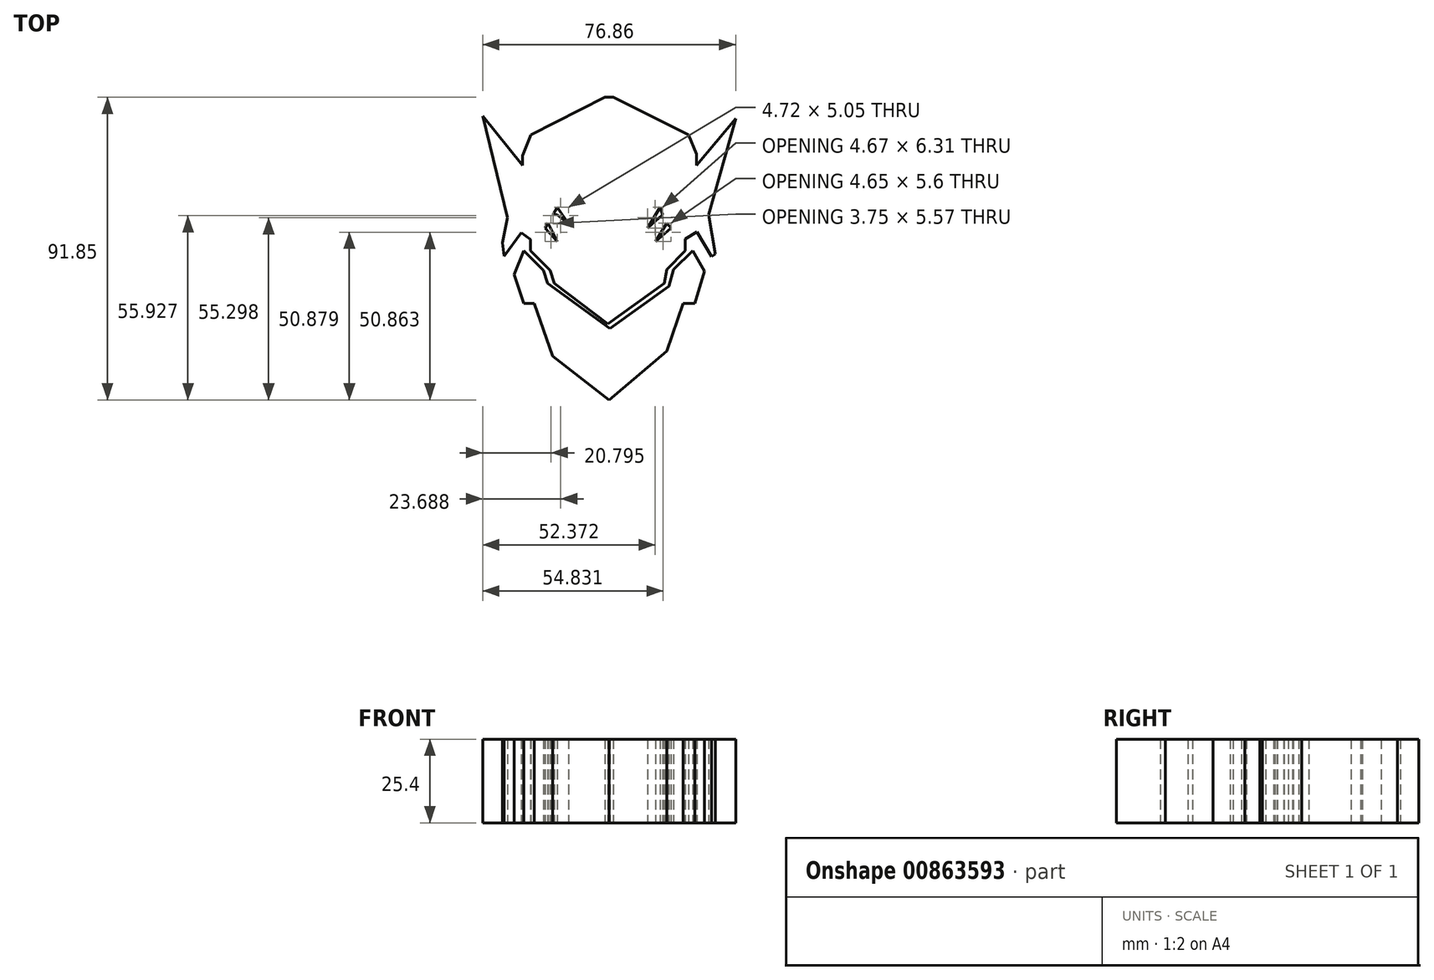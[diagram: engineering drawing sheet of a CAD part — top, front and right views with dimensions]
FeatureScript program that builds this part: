
annotation { "Feature Type Name" : "Feature", "Feature Type Description" : "" }
export const myFeature = defineFeature(function(context is Context, id is Id, definition is map)
    precondition{}
    {
        {
            var Q0;
            Q0=qCreatedBy(makeId("Top.planeOp"),FACE);
            var sketch = newSketch(context, id + "F0", { "sketchPlane" : qUnion([Q0])});
            skLineSegment(sketch, "E0", {"start": v(-37.07, 44.48) * mm, "end": v(-29.57, 13.63) * mm});
            skLineSegment(sketch, "E1", {"start": v(-29.57, 13.63) * mm, "end": v(-31.1, 5.96) * mm});
            skLineSegment(sketch, "E2", {"start": v(-31.1, 5.96) * mm, "end": v(-30.59, 1.87) * mm});
            skLineSegment(sketch, "E3", {"start": v(-30.59, 1.87) * mm, "end": v(-25.3, 9.03) * mm});
            skLineSegment(sketch, "E4", {"start": v(-25.3, 9.03) * mm, "end": v(-22.54, 6.99) * mm});
            skLineSegment(sketch, "E5", {"start": v(-22.54, 6.99) * mm, "end": v(-22.54, 3.58) * mm});
            skLineSegment(sketch, "E6", {"start": v(-22.54, 3.58) * mm, "end": v(-16.62, -2.39) * mm});
            skLineSegment(sketch, "E7", {"start": v(-16.62, -2.39) * mm, "end": v(-15.25, -6.3) * mm});
            skLineSegment(sketch, "E8", {"start": v(-15.25, -6.3) * mm, "end": v(0.9, -18.64) * mm});
            skLineSegment(sketch, "E9", {"start": v(0.9, -18.64) * mm, "end": v(18.07, -6.3) * mm});
            skLineSegment(sketch, "E10", {"start": v(18.07, -6.3) * mm, "end": v(18.83, -2.22) * mm});
            skLineSegment(sketch, "E11", {"start": v(18.83, -2.22) * mm, "end": v(24.45, 3.58) * mm});
            skLineSegment(sketch, "E12", {"start": v(24.45, 3.58) * mm, "end": v(24.45, 7.12) * mm});
            skLineSegment(sketch, "E13", {"start": v(24.45, 7.12) * mm, "end": v(27.95, 9.22) * mm});
            skLineSegment(sketch, "E14", {"start": v(27.95, 9.22) * mm, "end": v(32.39, 1.83) * mm});
            skLineSegment(sketch, "E15", {"start": v(32.39, 1.83) * mm, "end": v(33.6, 2.55) * mm});
            skLineSegment(sketch, "E16", {"start": v(33.6, 2.55) * mm, "end": v(31.61, 14.49) * mm});
            skLineSegment(sketch, "E17", {"start": v(31.61, 14.49) * mm, "end": v(39.8, 43.63) * mm});
            skLineSegment(sketch, "E18", {"start": v(39.8, 43.63) * mm, "end": v(27.86, 29.48) * mm});
            skLineSegment(sketch, "E19", {"start": v(27.86, 29.48) * mm, "end": v(27.86, 32.9) * mm});
            skLineSegment(sketch, "E20", {"start": v(27.86, 32.9) * mm, "end": v(25.48, 38.68) * mm});
            skLineSegment(sketch, "E21", {"start": v(25.48, 38.68) * mm, "end": v(2.64, 50.1) * mm});
            skLineSegment(sketch, "E22", {"start": v(2.64, 50.1) * mm, "end": v(0, 50.1) * mm});
            skLineSegment(sketch, "E23", {"start": v(0, 50.1) * mm, "end": v(-22.4, 38.68) * mm});
            skLineSegment(sketch, "E24", {"start": v(-22.4, 38.68) * mm, "end": v(-24.97, 32.38) * mm});
            skLineSegment(sketch, "E25", {"start": v(-24.97, 32.38) * mm, "end": v(-24.97, 29.48) * mm});
            skLineSegment(sketch, "E26", {"start": v(-24.97, 29.48) * mm, "end": v(-37.07, 44.48) * mm});
            skLineSegment(sketch, "E27", {"start": v(-29.57, 13.63) * mm, "end": v(-28.2, 18.58) * mm});
            skLineSegment(sketch, "E28", {"start": v(-28.2, 18.58) * mm, "end": v(-20.02, 25.73) * mm});
            skLineSegment(sketch, "E29", {"start": v(-20.02, 25.73) * mm, "end": v(-14.4, 22.32) * mm});
            skLineSegment(sketch, "E30", {"start": v(-14.4, 22.32) * mm, "end": v(1.45, 41.24) * mm});
            skLineSegment(sketch, "E31", {"start": v(1.45, 41.24) * mm, "end": v(17.3, 22.15) * mm});
            skLineSegment(sketch, "E32", {"start": v(17.3, 22.15) * mm, "end": v(23.77, 25.73) * mm});
            skLineSegment(sketch, "E33", {"start": v(23.77, 25.73) * mm, "end": v(30.42, 19.09) * mm});
            skLineSegment(sketch, "E34", {"start": v(30.42, 19.09) * mm, "end": v(31.61, 14.49) * mm});
            skLineSegment(sketch, "E35", {"start": v(-14.4, 14.49) * mm, "end": v(-11.02, 11.65) * mm});
            skLineSegment(sketch, "E36", {"start": v(-11.02, 11.65) * mm, "end": v(-14.4, 16.7) * mm});
            skLineSegment(sketch, "E37", {"start": v(-14.4, 16.7) * mm, "end": v(-15.74, 14.49) * mm});
            skLineSegment(sketch, "E38", {"start": v(-15.74, 14.49) * mm, "end": v(-14.4, 14.49) * mm});
            skLineSegment(sketch, "E39", {"start": v(-18.15, 10.4) * mm, "end": v(-17.24, 11.9) * mm});
            skLineSegment(sketch, "E40", {"start": v(-17.24, 11.9) * mm, "end": v(-14.4, 6.33) * mm});
            skLineSegment(sketch, "E41", {"start": v(-14.4, 6.33) * mm, "end": v(-18.15, 10.4) * mm});
            skLineSegment(sketch, "E42", {"start": v(16.79, 16.7) * mm, "end": v(12.96, 10.4) * mm});
            skLineSegment(sketch, "E43", {"start": v(12.96, 10.4) * mm, "end": v(17.64, 14.49) * mm});
            skLineSegment(sketch, "E44", {"start": v(17.64, 14.49) * mm, "end": v(16.79, 16.7) * mm});
            skLineSegment(sketch, "E45", {"start": v(18.83, 11.93) * mm, "end": v(15.44, 6.33) * mm});
            skLineSegment(sketch, "E46", {"start": v(15.44, 6.33) * mm, "end": v(20.08, 10.4) * mm});
            skLineSegment(sketch, "E47", {"start": v(20.08, 10.4) * mm, "end": v(18.83, 11.93) * mm});
            skLineSegment(sketch, "E48", {"start": v(-24.63, -12.44) * mm, "end": v(-21.39, -12.44) * mm});
            skLineSegment(sketch, "E49", {"start": v(-21.39, -12.44) * mm, "end": v(-15.76, -28.46) * mm});
            skLineSegment(sketch, "E50", {"start": v(-15.76, -28.46) * mm, "end": v(1.28, -41.75) * mm});
            skLineSegment(sketch, "E51", {"start": v(1.28, -41.75) * mm, "end": v(18.83, -26.93) * mm});
            skLineSegment(sketch, "E52", {"start": v(18.83, -26.93) * mm, "end": v(23.77, -12.44) * mm});
            skLineSegment(sketch, "E53", {"start": v(23.77, -12.44) * mm, "end": v(27.35, -12.44) * mm});
            skLineSegment(sketch, "E54", {"start": v(27.35, -12.44) * mm, "end": v(30.25, -2.73) * mm});
            skLineSegment(sketch, "E55", {"start": v(30.25, -2.73) * mm, "end": v(26.67, 3.58) * mm});
            skLineSegment(sketch, "E56", {"start": v(26.67, 3.58) * mm, "end": v(20.88, -2.22) * mm});
            skLineSegment(sketch, "E57", {"start": v(20.88, -2.22) * mm, "end": v(19.47, -7.22) * mm});
            skLineSegment(sketch, "E58", {"start": v(19.47, -7.22) * mm, "end": v(1.62, -20.1) * mm});
            skLineSegment(sketch, "E59", {"start": v(1.62, -20.1) * mm, "end": v(-17.3, -6.3) * mm});
            skLineSegment(sketch, "E60", {"start": v(-17.3, -6.3) * mm, "end": v(-18.67, -2.39) * mm});
            skLineSegment(sketch, "E61", {"start": v(-18.67, -2.39) * mm, "end": v(-24.63, 3.58) * mm});
            skLineSegment(sketch, "E62", {"start": v(-24.63, 3.58) * mm, "end": v(-27.52, -3.75) * mm});
            skLineSegment(sketch, "E63", {"start": v(-27.52, -3.75) * mm, "end": v(-24.63, -12.44) * mm});
            skLineSegment(sketch, "E64", {"start": v(-22.54, 6.99) * mm, "end": v(0, -12.47) * mm});
            skPoint(sketch, "E64.endSnap0", {"position": v(9.49, -12.47) * mm});
            skLineSegment(sketch, "E65", {"start": v(0, -12.47) * mm, "end": v(24.45, 7.12) * mm});
            skSolve(sketch);
        }
        {
            var Q0;
            Q0=makeQuery(id+"F0.imprint","IMPRINT",FACE,{"disambiguationData":[TD([[makeQuery(id+"F0.imprint","IMPRINT",EDGE,{"derivedFrom":sQuery(id+"F0.wireOp",EDGE,"E48")}),1.0]])]});
            var Q1;
            Q1=makeQuery(id+"F0.imprint","IMPRINT",FACE,{"disambiguationData":[TD([[makeQuery(id+"F0.imprint","IMPRINT",EDGE,{"derivedFrom":sQuery(id+"F0.wireOp",EDGE,"E5")}),1.0]])]});
            var Q2;
            Q2=makeQuery(id+"F0.imprint","IMPRINT",FACE,{"disambiguationData":[TD([[makeQuery(id+"F0.imprint","IMPRINT",EDGE,{"derivedFrom":sQuery(id+"F0.wireOp",EDGE,"E1")}),1.0]])]});
            var Q3;
            Q3=makeQuery(id+"F0.imprint","IMPRINT",FACE,{"disambiguationData":[TD([[makeQuery(id+"F0.imprint","IMPRINT",EDGE,{"derivedFrom":sQuery(id+"F0.wireOp",EDGE,"E0")}),1.0]])]});
            extrude(context, id + "F1", {"entities" : qUnion([Q0, Q1, Q2, Q3]), "depth" : 25.4 * mm, "offsetDistance" : 25.4 * mm});
        }
    });
